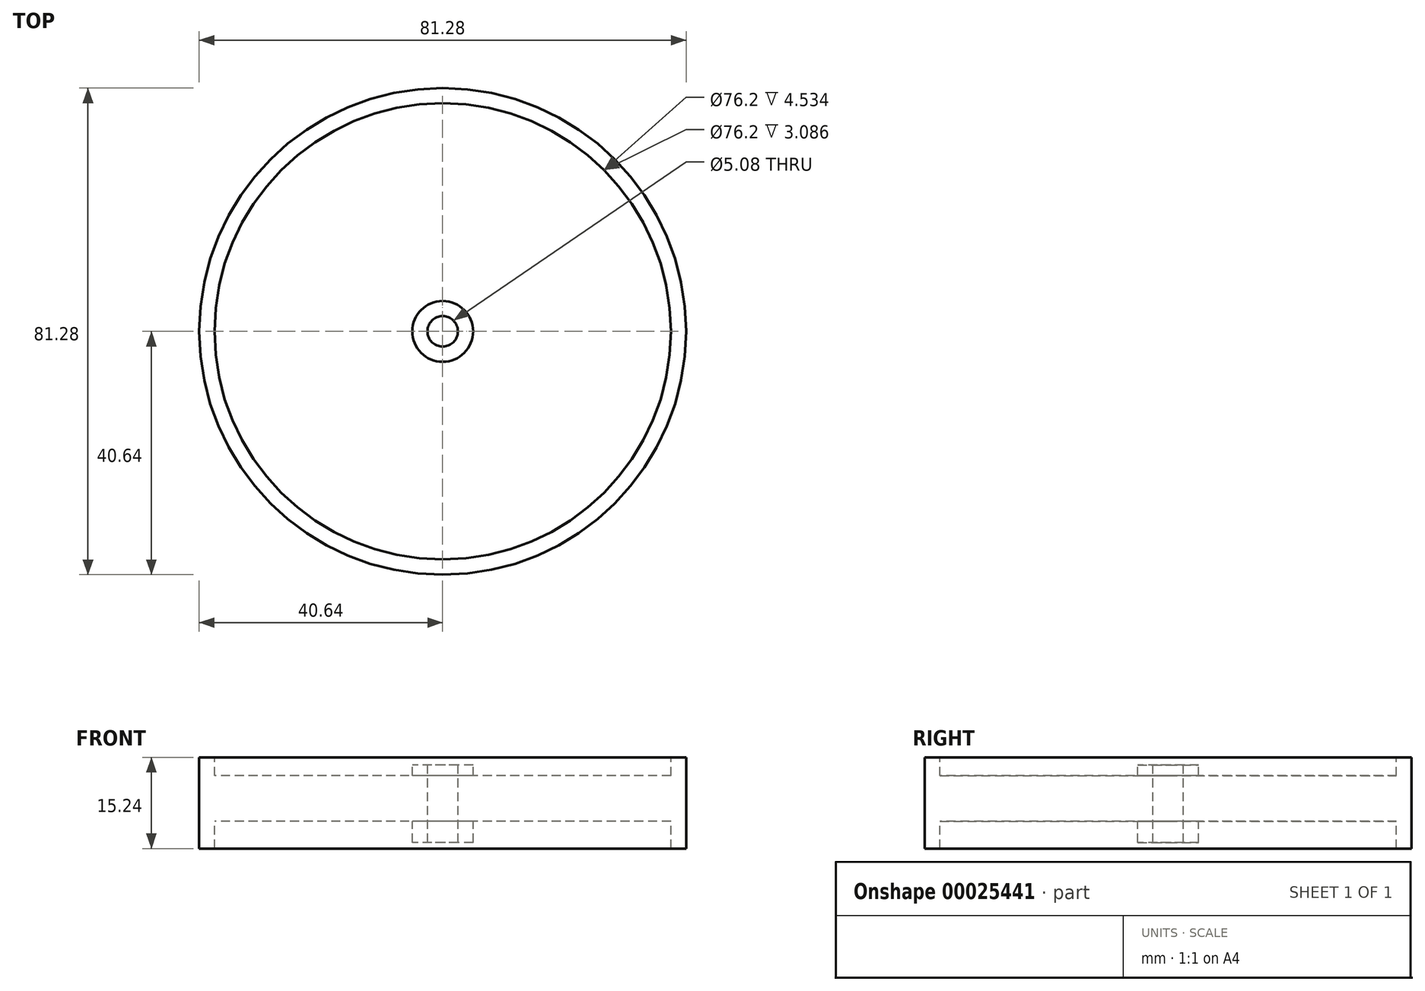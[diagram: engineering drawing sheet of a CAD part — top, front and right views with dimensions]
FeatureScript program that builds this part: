
annotation { "Feature Type Name" : "Feature", "Feature Type Description" : "" }
export const myFeature = defineFeature(function(context is Context, id is Id, definition is map)
    precondition{}
    {
        {
            var Q0;
            Q0=qCreatedBy(makeId("Front.planeOp"),FACE);
            var sketch = newSketch(context, id + "F0", { "sketchPlane" : qUnion([Q0])});
            skLineSegment(sketch, "E0", {"start": v(0, 21.85) * mm, "end": v(0, -19.59) * mm});
            skLineSegment(sketch, "E1.rect.bottom", {"start": v(2.54, 6.49) * mm, "end": v(5.08, 6.49) * mm});
            skLineSegment(sketch, "E1.rect.top", {"start": v(2.54, -6.49) * mm, "end": v(5.08, -6.49) * mm});
            skLineSegment(sketch, "E1.rect.left", {"start": v(2.54, 6.49) * mm, "end": v(2.54, -6.49) * mm});
            skLineSegment(sketch, "E1.rect.right", {"start": v(5.08, 6.49) * mm, "end": v(5.08, -6.49) * mm});
            skPoint(sketch, "E1.rect.middle", {"position": v(3.81, 0) * mm});
            skLineSegment(sketch, "E2.left", {"start": v(5.08, -2.96) * mm, "end": v(5.08, 4.66) * mm});
            skLineSegment(sketch, "E2.right", {"start": v(38.1, -2.96) * mm, "end": v(38.1, 4.66) * mm});
            skLineSegment(sketch, "E3.bottom", {"start": v(40.64, -7.5) * mm, "end": v(38.1, -7.5) * mm});
            skLineSegment(sketch, "E3.top", {"start": v(40.64, 7.75) * mm, "end": v(38.1, 7.75) * mm});
            skLineSegment(sketch, "E3.left", {"start": v(40.64, -7.5) * mm, "end": v(40.64, 7.75) * mm});
            skLineSegment(sketch, "E3.right", {"start": v(38.1, -7.5) * mm, "end": v(38.1, 7.75) * mm});
            skLineSegment(sketch, "E4.bottom", {"start": v(5.08, 4.66) * mm, "end": v(38.1, 4.66) * mm});
            skLineSegment(sketch, "E4.top", {"start": v(5.08, -2.96) * mm, "end": v(38.1, -2.96) * mm});
            skLineSegment(sketch, "E4.left", {"start": v(5.08, 4.66) * mm, "end": v(5.08, -2.96) * mm});
            skLineSegment(sketch, "E4.right", {"start": v(38.1, 4.66) * mm, "end": v(38.1, -2.96) * mm});
            skSolve(sketch);
        }
        {
            var Q0;
            Q0 = qSketchRegion(id + "F0", true);
            var Q1;
            Q1=sQuery(id+"F0.wireOp",EDGE,"E0");
            revolve(context, id + "F1", {"entities" : qUnion([Q0]), "axis" : qUnion([Q1]), "revolveType" : RevolveType.FULL});
        }
    });
